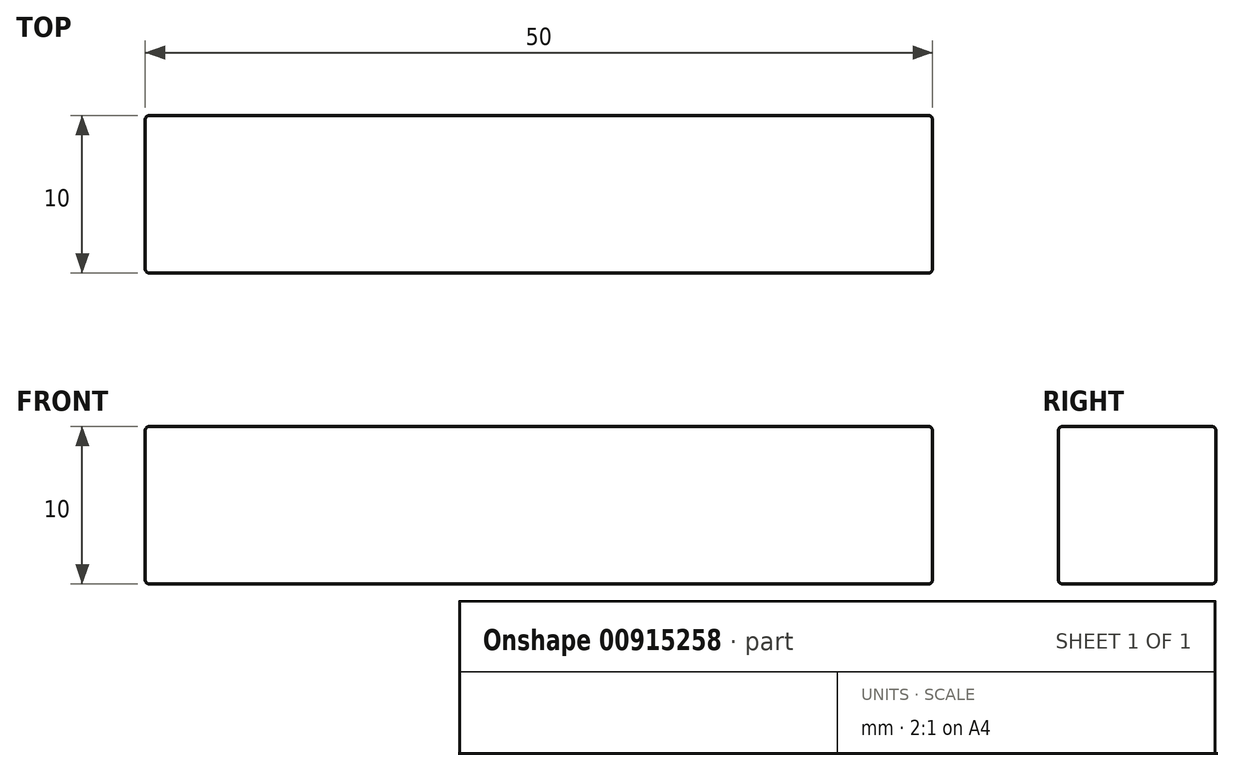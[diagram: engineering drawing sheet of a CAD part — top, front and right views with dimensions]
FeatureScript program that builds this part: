
annotation { "Feature Type Name" : "Feature", "Feature Type Description" : "" }
export const myFeature = defineFeature(function(context is Context, id is Id, definition is map)
    precondition{}
    {
        {
            var Q0;
            Q0=qCreatedBy(makeId("Front.planeOp"),FACE);
            var sketch = newSketch(context, id + "F0", { "sketchPlane" : qUnion([Q0])});
            skLineSegment(sketch, "E0.bottom", {"start": v(25, -5) * mm, "end": v(-25, -5) * mm});
            skLineSegment(sketch, "E0.top", {"start": v(25, 5) * mm, "end": v(-25, 5) * mm});
            skLineSegment(sketch, "E0.left", {"start": v(25, -5) * mm, "end": v(25, 5) * mm});
            skLineSegment(sketch, "E0.right", {"start": v(-25, -5) * mm, "end": v(-25, 5) * mm});
            skPoint(sketch, "E0.middle", {"position": v(0, 0) * mm});
            skSolve(sketch);
        }
        {
            var Q0;
            Q0=makeQuery(id+"F0.imprint","IMPRINT",FACE,{"disambiguationData":[TD([[makeQuery(id+"F0.imprint","IMPRINT",EDGE,{"derivedFrom":sQuery(id+"F0.wireOp",EDGE,"E0.bottom")}),-1.0]])]});
            extrude(context, id + "F1", {"entities" : qUnion([Q0]), "depth" : 5 * mm, "offsetDistance" : 25 * mm, "hasSecondDirection" : true, "secondDirectionOppositeDirection" : true, "secondDirectionDepth" : 5 * mm});
        }
        {
            var Q0;
            Q0=makeQuery(id+"F1.opExtrude","CAP_FACE",FACE,{"disambiguationData":[OSD([sQuery(id+"F0.wireOp",EDGE,"E0.bottom"),sQuery(id+"F0.wireOp",EDGE,"E0.top"),sQuery(id+"F0.wireOp",EDGE,"E0.left"),sQuery(id+"F0.wireOp",EDGE,"E0.right")])],"isStart":false});
            var Q1;
            Q1=makeQuery(id+"F1.opExtrude","CAP_FACE",FACE,{"disambiguationData":[OSD([sQuery(id+"F0.wireOp",EDGE,"E0.bottom"),sQuery(id+"F0.wireOp",EDGE,"E0.top"),sQuery(id+"F0.wireOp",EDGE,"E0.left"),sQuery(id+"F0.wireOp",EDGE,"E0.right")])],"isStart":true});
            var Q2;
            Q2=makeQuery(id+"F1.opExtrude","SWEPT_FACE",FACE,{"disambiguationData":[OSD([sQuery(id+"F0.wireOp",EDGE,"E0.left")])]});
            var Q3;
            Q3=makeQuery(id+"F1.opExtrude","SWEPT_FACE",FACE,{"disambiguationData":[OSD([sQuery(id+"F0.wireOp",EDGE,"E0.right")])]});
            fillet(context, id + "F2", {"entities" : qUnion([Q0, Q1, Q2, Q3]), "radius" : .25 * mm, "tangentPropagation" : true, "allowEdgeOverflow" : false});
        }
    });
